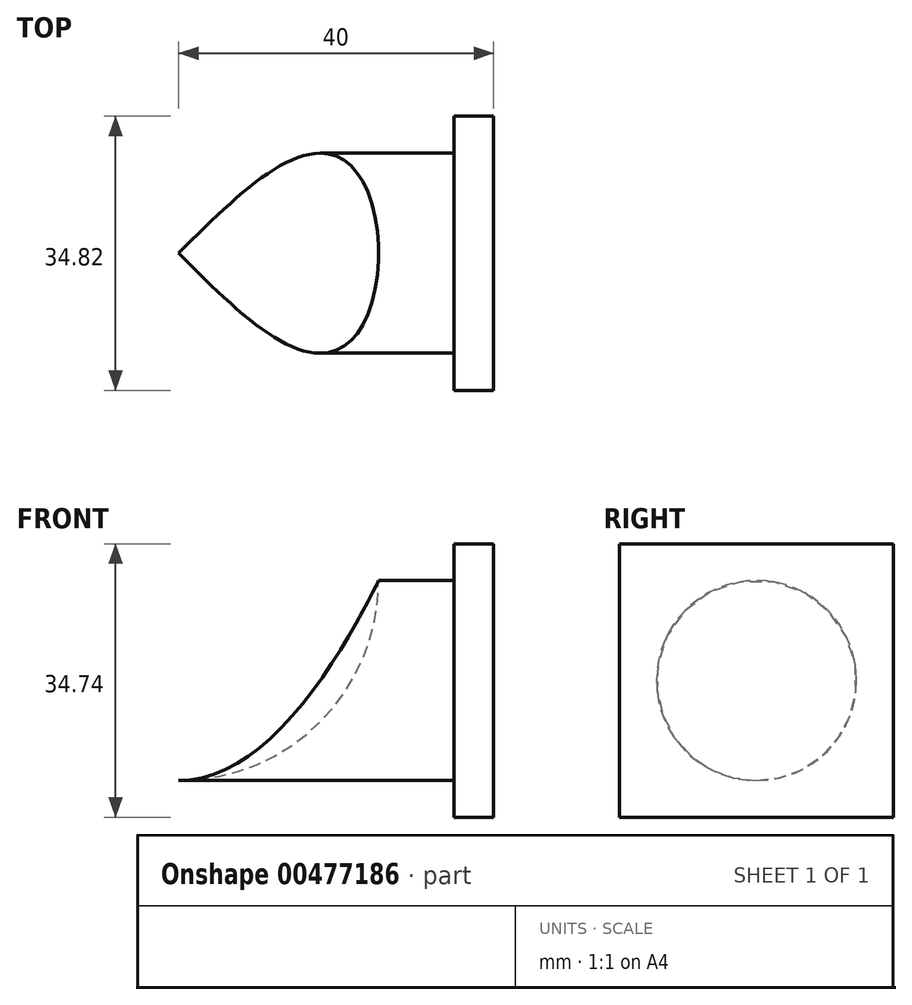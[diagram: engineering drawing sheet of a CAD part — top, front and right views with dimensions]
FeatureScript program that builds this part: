
annotation { "Feature Type Name" : "Feature", "Feature Type Description" : "" }
export const myFeature = defineFeature(function(context is Context, id is Id, definition is map)
    precondition{}
    {
        {
            var Q0;
            Q0=qCreatedBy(makeId("Right.planeOp"),FACE);
            var sketch = newSketch(context, id + "F0", { "sketchPlane" : qUnion([Q0])});
            skCircle(sketch, "E0", {"center": v(0, 0) * mm, "radius": 12.7 * mm});
            skSolve(sketch);
        }
        {
            var Q0;
            Q0=qSketchRegion(id+"F0",true);
            extrude(context, id + "F1", {"entities" : qUnion([Q0]), "depth" : 35 * mm});
        }
        {
            var Q0;
            Q0=makeQuery(id+"F1.opExtrude","CAP_FACE",FACE,{"disambiguationData":[OSD([sQuery(id+"F0.wireOp",EDGE,"E0")])],"isStart":false});
            var sketch = newSketch(context, id + "F2", { "sketchPlane" : qUnion([Q0])});
            skLineSegment(sketch, "E1.bottom", {"start": v(17.4, -17.37) * mm, "end": v(-17.4, -17.37) * mm});
            skLineSegment(sketch, "E1.top", {"start": v(17.4, 17.37) * mm, "end": v(-17.4, 17.37) * mm});
            skLineSegment(sketch, "E1.left", {"start": v(17.4, -17.37) * mm, "end": v(17.4, 17.37) * mm});
            skLineSegment(sketch, "E1.right", {"start": v(-17.4, -17.37) * mm, "end": v(-17.4, 17.37) * mm});
            skPoint(sketch, "E1.middle", {"position": v(0, 0) * mm});
            skSolve(sketch);
        }
        {
            var Q0;
            Q0=qSketchRegion(id+"F2",true);
            extrude(context, id + "F3", {"entities" : qUnion([Q0]), "operationType" : NewBodyOperationType.ADD, "depth" : 5 * mm});
        }
        {
            var Q0;
            Q0=makeQuery(id+"F1.opExtrude","CAP_FACE",FACE,{"disambiguationData":[OSD([sQuery(id+"F0.wireOp",EDGE,"E0")])],"isStart":true});
            var sketch = newSketch(context, id + "F4", { "sketchPlane" : qUnion([Q0])});
            skArc(sketch, "E2", {"start": v(0, -12.7) * mm, "mid": v(-25.4, 12.7) * mm, "end": v(0, 38.1) * mm});
            skLineSegment(sketch, "E3", {"start": v(0, -12.7) * mm, "end": v(0, 38.1) * mm});
            skSolve(sketch);
        }
        {
            var Q0;
            Q0 = qSketchRegion(id + "F4", true);
            var Q1;
            Q1=sQuery(id+"F4.wireOp",EDGE,"E3");
            revolve(context, id + "F5", {"operationType" : NewBodyOperationType.REMOVE, "entities" : qUnion([Q0]), "axis" : qUnion([Q1]), "revolveType" : RevolveType.FULL, "oppositeDirection" : true});
        }
    });
